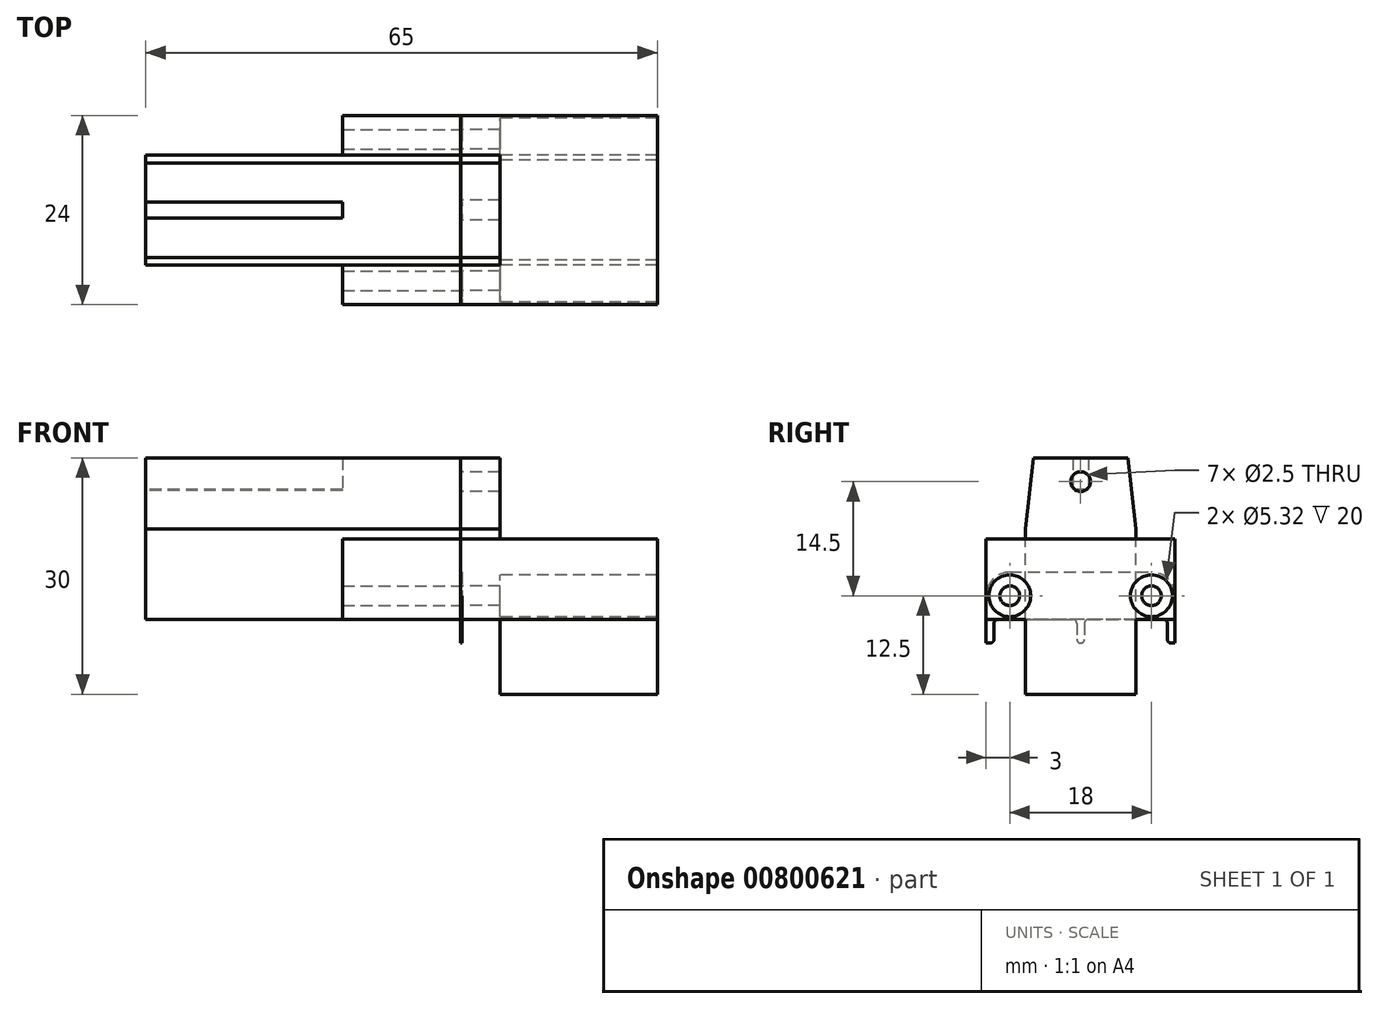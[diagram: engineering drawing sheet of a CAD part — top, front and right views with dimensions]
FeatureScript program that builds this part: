
annotation { "Feature Type Name" : "Feature", "Feature Type Description" : "" }
export const myFeature = defineFeature(function(context is Context, id is Id, definition is map)
    precondition{}
    {
        {
            var Q0;
            Q0=qCreatedBy(makeId("Right.planeOp"),FACE);
            var sketch = newSketch(context, id + "F0", { "sketchPlane" : qUnion([Q0])});
            skPoint(sketch, "E0", {"position": v(0, 13) * mm});
            skLineSegment(sketch, "E1", {"start": v(-44.38, 1.5) * mm, "end": v(56.51, 1.5) * mm, "construction": true});
            skCircle(sketch, "E2", {"center": v(0, 13) * mm, "radius": 5 * mm, "construction": true});
            skLineSegment(sketch, "E3.bottom", {"start": v(-7, 1.5) * mm, "end": v(7, 1.5) * mm});
            skLineSegment(sketch, "E3.top", {"start": v(-7, 22) * mm, "end": v(7, 22) * mm});
            skLineSegment(sketch, "E3.left", {"start": v(-7, 1.5) * mm, "end": v(-7, 22) * mm});
            skLineSegment(sketch, "E3.right", {"start": v(7, 1.5) * mm, "end": v(7, 22) * mm});
            skLineSegment(sketch, "E4", {"start": v(0, 33.56) * mm, "end": v(0, -8.49) * mm, "construction": true});
            skPoint(sketch, "E5", {"position": v(0, 22) * mm});
            skLineSegment(sketch, "E6.bottom", {"start": v(-7, 11.75) * mm, "end": v(-12, 11.75) * mm});
            skLineSegment(sketch, "E6.top", {"start": v(-7, 1.5) * mm, "end": v(-12, 1.5) * mm});
            skLineSegment(sketch, "E6.left", {"start": v(-7, 11.75) * mm, "end": v(-7, 1.5) * mm});
            skLineSegment(sketch, "E6.right", {"start": v(-12, 11.75) * mm, "end": v(-12, 1.5) * mm});
            skLineSegment(sketch, "E7.MirrorCS", {"start": v(12, 11.75) * mm, "end": v(12, 1.5) * mm});
            skLineSegment(sketch, "E8.MirrorCS", {"start": v(7, 11.75) * mm, "end": v(12, 11.75) * mm});
            skLineSegment(sketch, "E9.MirrorCS", {"start": v(7, 1.5) * mm, "end": v(12, 1.5) * mm});
            skCircle(sketch, "E10", {"center": v(-9, 4.5) * mm, "radius": 2.66 * mm, "construction": true});
            skCircle(sketch, "E11", {"center": v(-9, 4.5) * mm, "radius": 1.5 * mm, "construction": true});
            skCircle(sketch, "E12", {"center": v(-9, 4.5) * mm, "radius": 1.25 * mm});
            skCircle(sketch, "E13.MirrorC", {"center": v(9, 4.5) * mm, "radius": 1.25 * mm});
            skCircle(sketch, "E14.MirrorC", {"center": v(9, 4.5) * mm, "radius": 1.5 * mm, "construction": true});
            skCircle(sketch, "E15.MirrorC", {"center": v(9, 4.5) * mm, "radius": 2.66 * mm, "construction": true});
            skCircle(sketch, "E16", {"center": v(0, 19) * mm, "radius": 2.66 * mm, "construction": true});
            skCircle(sketch, "E17", {"center": v(0, 19) * mm, "radius": 1.5 * mm, "construction": true});
            skCircle(sketch, "E18", {"center": v(0, 19) * mm, "radius": 1.25 * mm});
            skLineSegment(sketch, "E19", {"start": v(-9.13, 13) * mm, "end": v(11.86, 13) * mm, "construction": true});
            skLineSegment(sketch, "E20", {"start": v(-7, 13) * mm, "end": v(-6, 22) * mm});
            skLineSegment(sketch, "E21.MirrorCS", {"start": v(7, 13) * mm, "end": v(6, 22) * mm});
            skSolve(sketch);
        }
        {
            var Q0;
            {var subQ1=sQuery(id+"F0.wireOp",EDGE,"E3.bottom");Q0=makeQuery(id+"F0.imprint","IMPRINT",FACE,{"disambiguationData":[TD([[makeQuery(id+"F0.imprint","IMPRINT",EDGE,{"derivedFrom":subQ1}),1.0]])]});}
            var Q1;
            Q1=makeQuery(id+"F0.imprint","IMPRINT",FACE,{"disambiguationData":[TD([[makeQuery(id+"F0.imprint","IMPRINT",EDGE,{"derivedFrom":sQuery(id+"F0.wireOp",EDGE,"E18")}),1.0]])]});
            extrude(context, id + "F1", {"entities" : qUnion([Q0, Q1]), "oppositeDirection" : true, "depth" : 40 * mm, "offsetDistance" : 25 * mm});
        }
        {
            var Q0;
            Q0=makeQuery(id+"F0.imprint","IMPRINT",FACE,{"disambiguationData":[TD([[makeQuery(id+"F0.imprint","IMPRINT",EDGE,{"derivedFrom":sQuery(id+"F0.wireOp",EDGE,"E6.bottom")}),1.0]])]});
            var Q1;
            Q1=makeQuery(id+"F0.imprint","IMPRINT",FACE,{"disambiguationData":[TD([[makeQuery(id+"F0.imprint","IMPRINT",EDGE,{"derivedFrom":sQuery(id+"F0.wireOp",EDGE,"E7.MirrorCS")}),-1.0]])]});
            extrude(context, id + "F2", {"entities" : qUnion([Q0, Q1]), "operationType" : NewBodyOperationType.ADD, "oppositeDirection" : true, "depth" : 15 * mm, "offsetDistance" : 25 * mm});
        }
        {
            var Q0;
            Q0=makeQuery(id+"F1.opExtrude","CAP_FACE",FACE,{"disambiguationData":[OSD([sQuery(id+"F0.wireOp",EDGE,"E3.bottom"),sQuery(id+"F0.wireOp",EDGE,"E3.top"),sQuery(id+"F0.wireOp",EDGE,"E3.left"),sQuery(id+"F0.wireOp",EDGE,"E3.right"),sQuery(id+"F0.wireOp",EDGE,"E6.left")])],"isStart":false});
            var sketch = newSketch(context, id + "F3", { "sketchPlane" : qUnion([Q0])});
            skCircle(sketch, "E22.0", {"center": v(0, 13) * mm, "radius": 5 * mm});
            skLineSegment(sketch, "E23.0", {"start": v(7, 22) * mm, "end": v(-7, 22) * mm});
            skLineSegment(sketch, "E24", {"start": v(-1, 22) * mm, "end": v(-1, 17.9) * mm});
            skLineSegment(sketch, "E25.MirrorCS", {"start": v(1, 22) * mm, "end": v(1, 17.9) * mm});
            skLineSegment(sketch, "E26", {"start": v(-9.44, 13) * mm, "end": v(9.03, 13) * mm, "construction": true});
            skLineSegment(sketch, "E27.0", {"start": v(-7, 1.5) * mm, "end": v(-7, 22) * mm});
            skLineSegment(sketch, "E28.0", {"start": v(7, 1.5) * mm, "end": v(7, 22) * mm});
            skSolve(sketch);
        }
        {
            var Q0;
            {var subQ0=sQuery(id+"F3.wireOp",EDGE,"E22.0");var subQ1=makeQuery(id+"F3.imprint","INTERSECT",VERTEX,{"derivedFrom":[subQ0,sQuery(id+"F3.wireOp",EDGE,"E24")]});Q0=makeQuery(id+"F3.imprint","IMPRINT",FACE,{"disambiguationData":[TD([[makeQuery(id+"F3.imprint","IMPRINT",EDGE,{"disambiguationData":[TD([[subQ1,1.0]])],"derivedFrom":subQ0}),-1.0]])]});}
            var Q1;
            {var subQ0=sQuery(id+"F3.wireOp",EDGE,"E24");Q1=makeQuery(id+"F3.imprint","IMPRINT",FACE,{"disambiguationData":[TD([[makeQuery(id+"F3.imprint","IMPRINT",EDGE,{"derivedFrom":subQ0}),1.0]])]});}
            extrude(context, id + "F4", {"entities" : qUnion([Q0, Q1]), "operationType" : NewBodyOperationType.REMOVE, "oppositeDirection" : true, "depth" : 25 * mm, "offsetDistance" : 25 * mm});
        }
        {
            var Q0;
            {var subQ0=sQuery(id+"F3.wireOp",EDGE,"E24");Q0=makeQuery(id+"F3.imprint","IMPRINT",FACE,{"disambiguationData":[TD([[makeQuery(id+"F3.imprint","IMPRINT",EDGE,{"derivedFrom":subQ0}),1.0]])]});}
            var Q1;
            {var subQ0=sQuery(id+"F3.wireOp",EDGE,"E22.0");var subQ1=makeQuery(id+"F3.imprint","INTERSECT",VERTEX,{"derivedFrom":[subQ0,sQuery(id+"F3.wireOp",EDGE,"E24")]});Q1=makeQuery(id+"F3.imprint","IMPRINT",FACE,{"disambiguationData":[TD([[makeQuery(id+"F3.imprint","IMPRINT",EDGE,{"disambiguationData":[TD([[subQ1,1.0]])],"derivedFrom":subQ0}),-1.0]])]});}
            extrude(context, id + "F5", {"entities" : qUnion([Q0, Q1]), "operationType" : NewBodyOperationType.REMOVE, "oppositeDirection" : true, "depth" : 25 * mm, "offsetDistance" : 25 * mm});
        }
        {
            var Q0;
            {var subQ0=sQuery(id+"F0.wireOp",EDGE,"E6.left");var subQ1=sQuery(id+"F0.wireOp",EDGE,"E3.right");Q0=makeQuery(id+"F2.boolean.opBoolean","MERGE",FACE,{"derivedFrom":[makeQuery(id+"F1.opExtrude","CAP_FACE",FACE,{"disambiguationData":[OSD([sQuery(id+"F0.wireOp",EDGE,"E3.bottom"),sQuery(id+"F0.wireOp",EDGE,"E3.top"),sQuery(id+"F0.wireOp",EDGE,"E3.left"),subQ1,subQ0])],"isStart":true}),makeQuery(id+"F2.opExtrude","CAP_FACE",FACE,{"disambiguationData":[OSD([subQ1,sQuery(id+"F0.wireOp",EDGE,"E7.MirrorCS"),sQuery(id+"F0.wireOp",EDGE,"E8.MirrorCS"),sQuery(id+"F0.wireOp",EDGE,"E9.MirrorCS"),sQuery(id+"F0.wireOp",EDGE,"E13.MirrorC")])],"isStart":true}),makeQuery(id+"F2.opExtrude","CAP_FACE",FACE,{"disambiguationData":[OSD([sQuery(id+"F0.wireOp",EDGE,"E6.bottom"),sQuery(id+"F0.wireOp",EDGE,"E6.top"),subQ0,sQuery(id+"F0.wireOp",EDGE,"E6.right"),sQuery(id+"F0.wireOp",EDGE,"E12")])],"isStart":true})]});}
            var sketch = newSketch(context, id + "F6", { "sketchPlane" : qUnion([Q0])});
            skLineSegment(sketch, "E29", {"start": v(-16.94, 0) * mm, "end": v(22.34, 0) * mm, "construction": true});
            skLineSegment(sketch, "E30.bottom", {"start": v(-12, 0) * mm, "end": v(12, 0) * mm});
            skLineSegment(sketch, "E30.top", {"start": v(-9, 7.5) * mm, "end": v(9, 7.5) * mm});
            skLineSegment(sketch, "E30.left", {"start": v(-12, 0) * mm, "end": v(-12, 4.5) * mm});
            skLineSegment(sketch, "E30.right", {"start": v(12, 0) * mm, "end": v(12, 4.5) * mm});
            skCircle(sketch, "E31.0", {"center": v(-9, 4.5) * mm, "radius": 1.25 * mm});
            skCircle(sketch, "E32.0", {"center": v(9, 4.5) * mm, "radius": 1.25 * mm});
            skPoint(sketch, "E33.visualSharp", {"position": v(-12, 7.5) * mm});
            skArc(sketch, "E33.filletArc", {"start": v(-9, 7.5) * mm, "mid": v(-11.12, 6.62) * mm, "end": v(-12, 4.5) * mm});
            skPoint(sketch, "E34.visualSharp", {"position": v(12, 7.5) * mm});
            skArc(sketch, "E34.filletArc", {"start": v(12, 4.5) * mm, "mid": v(11.12, 6.62) * mm, "end": v(9, 7.5) * mm});
            skLineSegment(sketch, "E35.MirrorCS", {"start": v(12, 0) * mm, "end": v(12, -4.5) * mm});
            skArc(sketch, "E36.MirrorCS", {"start": v(12, -4.5) * mm, "mid": v(11.12, -6.62) * mm, "end": v(9, -7.5) * mm});
            skLineSegment(sketch, "E37.MirrorCS", {"start": v(-9, -7.5) * mm, "end": v(9, -7.5) * mm});
            skArc(sketch, "E38.MirrorCS", {"start": v(-9, -7.5) * mm, "mid": v(-11.12, -6.62) * mm, "end": v(-12, -4.5) * mm});
            skLineSegment(sketch, "E39.MirrorCS", {"start": v(-12, 0) * mm, "end": v(-12, -4.5) * mm});
            skCircle(sketch, "E40.MirrorC", {"center": v(-9, -4.5) * mm, "radius": 1.25 * mm});
            skCircle(sketch, "E41.MirrorC", {"center": v(9, -4.5) * mm, "radius": 1.25 * mm});
            skLineSegment(sketch, "E42.0", {"start": v(-12, 1.5) * mm, "end": v(12, 1.5) * mm});
            skLineSegment(sketch, "E43", {"start": v(-11, 1.5) * mm, "end": v(-11, 0) * mm});
            skLineSegment(sketch, "E44", {"start": v(-0.5, 1.5) * mm, "end": v(-0.5, 0) * mm});
            skLineSegment(sketch, "E45", {"start": v(0, -12.77) * mm, "end": v(0, 23.76) * mm, "construction": true});
            skPoint(sketch, "E45.endSnap0", {"position": v(0, 22) * mm});
            skLineSegment(sketch, "E46.MirrorCS", {"start": v(0.5, 1.5) * mm, "end": v(0.5, 0) * mm});
            skLineSegment(sketch, "E47.MirrorCS", {"start": v(11, 1.5) * mm, "end": v(11, 0) * mm});
            skLineSegment(sketch, "E48.MirrorCS", {"start": v(-12, -1.5) * mm, "end": v(12, -1.5) * mm});
            skLineSegment(sketch, "E49.MirrorCS", {"start": v(-11, -1.5) * mm, "end": v(-11, 0) * mm});
            skLineSegment(sketch, "E50.MirrorCS", {"start": v(-0.5, -1.5) * mm, "end": v(-0.5, 0) * mm});
            skLineSegment(sketch, "E51.MirrorCS", {"start": v(0.5, -1.5) * mm, "end": v(0.5, 0) * mm});
            skLineSegment(sketch, "E52.MirrorCS", {"start": v(11, -1.5) * mm, "end": v(11, 0) * mm});
            skSolve(sketch);
        }
        {
            var Q0;
            Q0=makeQuery(id+"F6.imprint","IMPRINT",FACE,{"disambiguationData":[TD([[makeQuery(id+"F6.imprint","IMPRINT",EDGE,{"derivedFrom":sQuery(id+"F6.wireOp",EDGE,"E30.top")}),-1.0]])]});
            var Q1;
            {var subQ3=sQuery(id+"F6.wireOp",EDGE,"E43");Q1=makeQuery(id+"F6.imprint","IMPRINT",FACE,{"disambiguationData":[TD([[makeQuery(id+"F6.imprint","IMPRINT",EDGE,{"derivedFrom":subQ3}),-1.0]])]});}
            var Q2;
            {var subQ3=sQuery(id+"F6.wireOp",EDGE,"E49.MirrorCS");Q2=makeQuery(id+"F6.imprint","IMPRINT",FACE,{"disambiguationData":[TD([[makeQuery(id+"F6.imprint","IMPRINT",EDGE,{"derivedFrom":subQ3}),1.0]])]});}
            var Q3;
            {var subQ0=sQuery(id+"F6.wireOp",EDGE,"E44");Q3=makeQuery(id+"F6.imprint","IMPRINT",FACE,{"disambiguationData":[TD([[makeQuery(id+"F6.imprint","IMPRINT",EDGE,{"derivedFrom":subQ0}),1.0]])]});}
            var Q4;
            {var subQ0=sQuery(id+"F6.wireOp",EDGE,"E50.MirrorCS");Q4=makeQuery(id+"F6.imprint","IMPRINT",FACE,{"disambiguationData":[TD([[makeQuery(id+"F6.imprint","IMPRINT",EDGE,{"derivedFrom":subQ0}),-1.0]])]});}
            var Q5;
            {var subQ3=sQuery(id+"F6.wireOp",EDGE,"E47.MirrorCS");Q5=makeQuery(id+"F6.imprint","IMPRINT",FACE,{"disambiguationData":[TD([[makeQuery(id+"F6.imprint","IMPRINT",EDGE,{"derivedFrom":subQ3}),1.0]])]});}
            var Q6;
            {var subQ3=sQuery(id+"F6.wireOp",EDGE,"E52.MirrorCS");Q6=makeQuery(id+"F6.imprint","IMPRINT",FACE,{"disambiguationData":[TD([[makeQuery(id+"F6.imprint","IMPRINT",EDGE,{"derivedFrom":subQ3}),-1.0]])]});}
            var Q7;
            {var subQ7=sQuery(id+"F6.wireOp",EDGE,"E36.MirrorCS");Q7=makeQuery(id+"F6.imprint","IMPRINT",FACE,{"disambiguationData":[TD([[makeQuery(id+"F6.imprint","IMPRINT",EDGE,{"derivedFrom":subQ7}),-1.0]])]});}
            extrude(context, id + "F7", {"entities" : qUnion([Q0, Q1, Q2, Q3, Q4, Q5, Q6, Q7]), "depth" : 0.2 * mm, "offsetDistance" : 25 * mm});
        }
        {
            var Q0;
            Q0=makeQuery(id+"F7.opExtrude","SWEPT_EDGE",EDGE,{"disambiguationData":[OSD([sQuery(id+"F6.wireOp",EDGE,"E42.0"),sQuery(id+"F6.wireOp",EDGE,"E44")])]});
            var Q1;
            Q1=makeQuery(id+"F7.opExtrude","SWEPT_EDGE",EDGE,{"disambiguationData":[OSD([sQuery(id+"F6.wireOp",EDGE,"E42.0"),sQuery(id+"F6.wireOp",EDGE,"E43")])]});
            var Q2;
            Q2=makeQuery(id+"F7.opExtrude","SWEPT_EDGE",EDGE,{"disambiguationData":[OSD([sQuery(id+"F6.wireOp",EDGE,"E48.MirrorCS"),sQuery(id+"F6.wireOp",EDGE,"E50.MirrorCS")])]});
            var Q3;
            Q3=makeQuery(id+"F7.opExtrude","SWEPT_EDGE",EDGE,{"disambiguationData":[OSD([sQuery(id+"F6.wireOp",EDGE,"E48.MirrorCS"),sQuery(id+"F6.wireOp",EDGE,"E49.MirrorCS")])]});
            var Q4;
            Q4=makeQuery(id+"F7.opExtrude","SWEPT_EDGE",EDGE,{"disambiguationData":[OSD([sQuery(id+"F6.wireOp",EDGE,"E48.MirrorCS"),sQuery(id+"F6.wireOp",EDGE,"E51.MirrorCS")])]});
            var Q5;
            Q5=makeQuery(id+"F7.opExtrude","SWEPT_EDGE",EDGE,{"disambiguationData":[OSD([sQuery(id+"F6.wireOp",EDGE,"E42.0"),sQuery(id+"F6.wireOp",EDGE,"E47.MirrorCS")])]});
            var Q6;
            Q6=makeQuery(id+"F7.opExtrude","SWEPT_EDGE",EDGE,{"disambiguationData":[OSD([sQuery(id+"F6.wireOp",EDGE,"E42.0"),sQuery(id+"F6.wireOp",EDGE,"E46.MirrorCS")])]});
            var Q7;
            Q7=makeQuery(id+"F7.opExtrude","SWEPT_EDGE",EDGE,{"disambiguationData":[OSD([sQuery(id+"F6.wireOp",EDGE,"E48.MirrorCS"),sQuery(id+"F6.wireOp",EDGE,"E52.MirrorCS")])]});
            fillet(context, id + "F8", {"entities" : qUnion([Q0, Q1, Q2, Q3, Q4, Q5, Q6, Q7]), "tangentPropagation" : true, "radius" : 0.5 * mm, "defaultsChanged" : false, "vertexSettings" : [], "allowEdgeOverflow" : false});
        }
        {
            var Q0;
            Q0=makeQuery(id+"F0.imprint","IMPRINT",FACE,{"disambiguationData":[TD([[makeQuery(id+"F0.imprint","IMPRINT",EDGE,{"derivedFrom":sQuery(id+"F0.wireOp",EDGE,"E6.bottom")}),1.0]])]});
            var Q1;
            {var subQ1=sQuery(id+"F0.wireOp",EDGE,"E3.bottom");Q1=makeQuery(id+"F0.imprint","IMPRINT",FACE,{"disambiguationData":[TD([[makeQuery(id+"F0.imprint","IMPRINT",EDGE,{"derivedFrom":subQ1}),1.0]])]});}
            var Q2;
            Q2=makeQuery(id+"F0.imprint","IMPRINT",FACE,{"disambiguationData":[TD([[makeQuery(id+"F0.imprint","IMPRINT",EDGE,{"derivedFrom":sQuery(id+"F0.wireOp",EDGE,"E7.MirrorCS")}),-1.0]])]});
            extrude(context, id + "F9", {"entities" : qUnion([Q0, Q1, Q2]), "depth" : 5 * mm, "offsetDistance" : 25 * mm});
        }
        {
            var Q0;
            Q0=makeQuery(id+"F9.opExtrude","CAP_FACE",FACE,{"disambiguationData":[OSD([sQuery(id+"F0.wireOp",EDGE,"E3.bottom"),sQuery(id+"F0.wireOp",EDGE,"E3.top"),sQuery(id+"F0.wireOp",EDGE,"E3.left"),sQuery(id+"F0.wireOp",EDGE,"E3.right"),sQuery(id+"F0.wireOp",EDGE,"E6.bottom"),sQuery(id+"F0.wireOp",EDGE,"E6.top"),sQuery(id+"F0.wireOp",EDGE,"E6.right"),sQuery(id+"F0.wireOp",EDGE,"E7.MirrorCS"),sQuery(id+"F0.wireOp",EDGE,"E8.MirrorCS"),sQuery(id+"F0.wireOp",EDGE,"E9.MirrorCS"),sQuery(id+"F0.wireOp",EDGE,"E12"),sQuery(id+"F0.wireOp",EDGE,"E13.MirrorC"),sQuery(id+"F0.wireOp",EDGE,"E18"),sQuery(id+"F0.wireOp",EDGE,"E20"),sQuery(id+"F0.wireOp",EDGE,"E21.MirrorCS")])],"isStart":false});
            var sketch = newSketch(context, id + "F10", { "sketchPlane" : qUnion([Q0])});
            skCircle(sketch, "E53", {"center": v(0, 0) * mm, "radius": 5 * mm, "construction": true});
            skLineSegment(sketch, "E54.bottom", {"start": v(-7, 11.75) * mm, "end": v(7, 11.75) * mm});
            skLineSegment(sketch, "E54.top", {"start": v(-7, -8) * mm, "end": v(7, -8) * mm});
            skLineSegment(sketch, "E54.left", {"start": v(-7, 11.75) * mm, "end": v(-7, -8) * mm});
            skLineSegment(sketch, "E54.right", {"start": v(7, 11.75) * mm, "end": v(7, -8) * mm});
            skCircle(sketch, "E55.0", {"center": v(0, 19) * mm, "radius": 1.25 * mm});
            skCircle(sketch, "E56.0", {"center": v(-9, 4.5) * mm, "radius": 1.25 * mm});
            skCircle(sketch, "E57.0", {"center": v(9, 4.5) * mm, "radius": 1.25 * mm});
            skCircle(sketch, "E58", {"center": v(0, 19) * mm, "radius": 2.66 * mm});
            skCircle(sketch, "E59", {"center": v(-9, 4.5) * mm, "radius": 2.66 * mm});
            skCircle(sketch, "E60", {"center": v(9, 4.5) * mm, "radius": 2.66 * mm});
            skSolve(sketch);
        }
        {
            var Q0;
            {var subQ0=sQuery(id+"F10.wireOp",EDGE,"E54.top");Q0=makeQuery(id+"F10.imprint","IMPRINT",FACE,{"disambiguationData":[TD([[makeQuery(id+"F10.imprint","IMPRINT",EDGE,{"derivedFrom":subQ0}),1.0]])]});}
            var Q1;
            {var subQ1=sQuery(id+"F10.wireOp",EDGE,"E54.bottom");Q1=makeQuery(id+"F10.imprint","IMPRINT",FACE,{"disambiguationData":[TD([[makeQuery(id+"F10.imprint","IMPRINT",EDGE,{"derivedFrom":subQ1}),-1.0]])]});}
            var Q2;
            {var subQ0=makeQuery(id+"F9.opExtrude","CAP_EDGE",EDGE,{"disambiguationData":[OSD([sQuery(id+"F0.wireOp",EDGE,"E6.bottom")])],"isStart":false});Q2=makeQuery(id+"F10.imprint","IMPRINT",FACE,{"disambiguationData":[TD([[makeQuery(id+"F10.imprint","IMPRINT",EDGE,{"derivedFrom":subQ0}),1.0]])]});}
            var Q3;
            {var subQ5=makeQuery(id+"F9.opExtrude","CAP_EDGE",EDGE,{"disambiguationData":[OSD([sQuery(id+"F0.wireOp",EDGE,"E7.MirrorCS")])],"isStart":false});Q3=makeQuery(id+"F10.imprint","IMPRINT",FACE,{"disambiguationData":[TD([[makeQuery(id+"F10.imprint","IMPRINT",EDGE,{"derivedFrom":subQ5}),-1.0]])]});}
            extrude(context, id + "F11", {"entities" : qUnion([Q0, Q1, Q2, Q3]), "operationType" : NewBodyOperationType.ADD, "depth" : 20 * mm, "offsetDistance" : 25 * mm});
        }
    });
